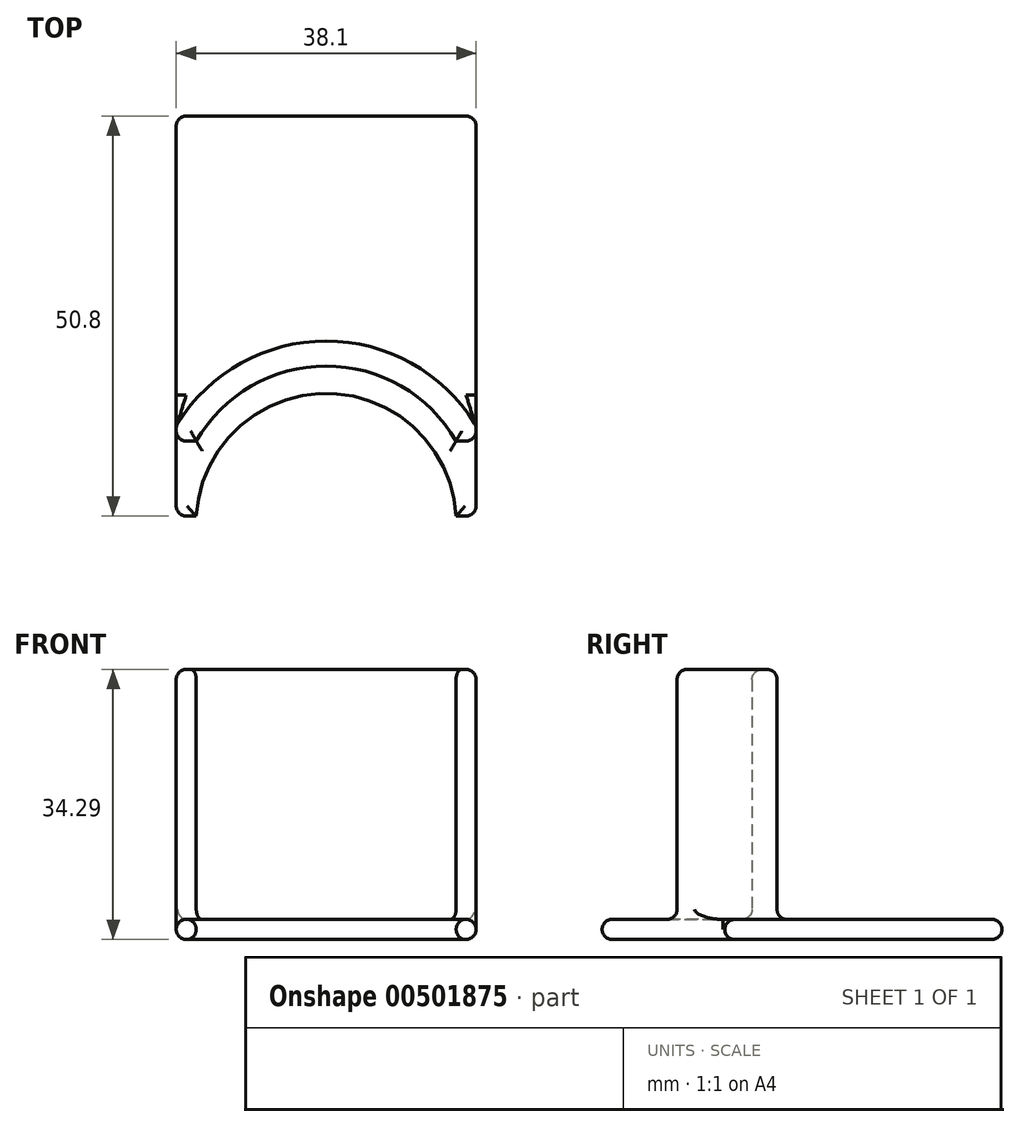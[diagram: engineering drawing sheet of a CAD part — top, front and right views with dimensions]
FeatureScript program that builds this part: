
annotation { "Feature Type Name" : "Feature", "Feature Type Description" : "" }
export const myFeature = defineFeature(function(context is Context, id is Id, definition is map)
    precondition{}
    {
        {
            var Q0;
            Q0=qCreatedBy(makeId("Top.planeOp"),FACE);
            var sketch = newSketch(context, id + "F0", { "sketchPlane" : qUnion([Q0])});
            skLineSegment(sketch, "E0.bottom", {"start": v(19.05, -19.05) * mm, "end": v(-19.05, -19.05) * mm});
            skLineSegment(sketch, "E0.top", {"start": v(19.05, 19.05) * mm, "end": v(-19.05, 19.05) * mm});
            skLineSegment(sketch, "E0.left", {"start": v(19.05, -19.05) * mm, "end": v(19.05, 19.05) * mm});
            skLineSegment(sketch, "E0.right", {"start": v(-19.05, -19.05) * mm, "end": v(-19.05, 19.05) * mm});
            skPoint(sketch, "E0.middle", {"position": v(0, 0) * mm});
            skSolve(sketch);
        }
        {
            var Q0;
            Q0=makeQuery(id+"F0.imprint","IMPRINT",FACE,{"disambiguationData":[TD([[makeQuery(id+"F0.imprint","IMPRINT",EDGE,{"derivedFrom":sQuery(id+"F0.wireOp",EDGE,"E0.bottom")}),-1.0]])]});
            extrude(context, id + "F1", {"entities" : qUnion([Q0]), "depth" : 2.54 * mm});
        }
        {
            var Q0;
            Q0=makeQuery(id+"F1.opExtrude","CAP_FACE",FACE,{"disambiguationData":[OSD([sQuery(id+"F0.wireOp",EDGE,"E0.bottom"),sQuery(id+"F0.wireOp",EDGE,"E0.top"),sQuery(id+"F0.wireOp",EDGE,"E0.left"),sQuery(id+"F0.wireOp",EDGE,"E0.right")])],"isStart":false});
            var sketch = newSketch(context, id + "F2", { "sketchPlane" : qUnion([Q0])});
            skArc(sketch, "E1", {"start": v(16.5, -9.52) * mm, "mid": v(0, 0) * mm, "end": v(-16.5, -9.53) * mm});
            skArc(sketch, "E2", {"start": v(16.5, -19.05) * mm, "mid": v(0, -3.48) * mm, "end": v(-16.51, -19.05) * mm});
            skLineSegment(sketch, "E3", {"start": v(16.5, -19.05) * mm, "end": v(-16.5, -19.05) * mm});
            skArc(sketch, "E4.0", {"start": v(19.05, -7.6) * mm, "mid": v(0, 3.18) * mm, "end": v(-19.05, -7.6) * mm});
            skLineSegment(sketch, "E5", {"start": v(19.05, -9.52) * mm, "end": v(19.05, -7.6) * mm});
            skLineSegment(sketch, "E6", {"start": v(-19.05, -9.52) * mm, "end": v(-19.05, -7.6) * mm});
            skLineSegment(sketch, "E7", {"start": v(19.05, -9.52) * mm, "end": v(16.5, -9.52) * mm});
            skLineSegment(sketch, "E8.trimOffspring", {"start": v(-16.5, -9.52) * mm, "end": v(-19.05, -9.52) * mm});
            skSolve(sketch);
        }
        {
            var Q0;
            Q0=makeQuery(id+"F2.imprint","IMPRINT",FACE,{"disambiguationData":[TD([[makeQuery(id+"F2.imprint","IMPRINT",EDGE,{"derivedFrom":sQuery(id+"F2.wireOp",EDGE,"E2")}),1.0]])]});
            extrude(context, id + "F3", {"entities" : qUnion([Q0]), "operationType" : NewBodyOperationType.REMOVE, "oppositeDirection" : true, "depth" : 25.4 * mm});
        }
        {
            var Q0;
            Q0=makeQuery(id+"F2.imprint","IMPRINT",FACE,{"disambiguationData":[TD([[makeQuery(id+"F2.imprint","IMPRINT",EDGE,{"derivedFrom":sQuery(id+"F2.wireOp",EDGE,"E1")}),-1.0]])]});
            extrude(context, id + "F4", {"entities" : qUnion([Q0]), "operationType" : NewBodyOperationType.ADD, "depth" : 31.75 * mm});
        }
        {
            var Q0;
            Q0=makeQuery(id+"F4.opExtrude","SWEPT_EDGE",EDGE,{"disambiguationData":[OSD([sQuery(id+"F0.wireOp",EDGE,"E0.left"),sQuery(id+"F2.wireOp",EDGE,"E5"),sQuery(id+"F2.wireOp",EDGE,"E7")])]});
            var Q1;
            Q1=makeQuery(id+"F4.opExtrude","SWEPT_EDGE",EDGE,{"disambiguationData":[OSD([sQuery(id+"F0.wireOp",EDGE,"E0.right"),sQuery(id+"F2.wireOp",EDGE,"E6"),sQuery(id+"F2.wireOp",EDGE,"E8.trimOffspring")])]});
            fillet(context, id + "F5", {"entities" : qUnion([Q0, Q1]), "radius" : 1.27 * mm, "tangentPropagation" : true, "allowEdgeOverflow" : false});
        }
        {
            var Q0;
            Q0=makeQuery(id+"F1.opExtrude","SWEPT_FACE",FACE,{"disambiguationData":[OSD([sQuery(id+"F0.wireOp",EDGE,"E0.top")])]});
            extrude(context, id + "F6", {"entities" : qUnion([Q0]), "operationType" : NewBodyOperationType.ADD, "depth" : 12.7 * mm});
        }
        {
            var Q0;
            {var subQ0=sQuery(id+"F0.wireOp",EDGE,"E0.top");var subQ1=sQuery(id+"F0.wireOp",EDGE,"E0.right");var subQ2=sQuery(id+"F0.wireOp",EDGE,"E0.left");Q0=makeQuery(id+"F6.boolean.opBoolean","MERGE",FACE,{"derivedFrom":[makeQuery(id+"F4.boolean.opBoolean","SPLIT",FACE,{"disambiguationData":[TD([makeQuery(id+"F1.opExtrude","SWEPT_FACE",FACE,{"disambiguationData":[OSD([subQ0])]})])],"derivedFrom":makeQuery(id+"F1.opExtrude","CAP_FACE",FACE,{"disambiguationData":[OSD([sQuery(id+"F0.wireOp",EDGE,"E0.bottom"),subQ0,subQ2,subQ1])],"isStart":false})}),makeQuery(id+"F6.opExtrude","SWEPT_FACE",FACE,{"disambiguationData":[OSD([subQ0]),TDD([makeQuery(id+"F1.opExtrude","CAP_EDGE",EDGE,{"disambiguationData":[OSD([subQ0])],"isStart":false})])]})]});}
            var Q1;
            {var subQ0=sQuery(id+"F0.wireOp",EDGE,"E0.left");Q1=makeQuery(id+"F6.boolean.opBoolean","MERGE",FACE,{"derivedFrom":[makeQuery(id+"F4.boolean.opBoolean","MERGE",FACE,{"derivedFrom":[makeQuery(id+"F1.opExtrude","SWEPT_FACE",FACE,{"disambiguationData":[OSD([subQ0])]}),makeQuery(id+"F4.opExtrude","SWEPT_FACE",FACE,{"disambiguationData":[OSD([sQuery(id+"F2.wireOp",EDGE,"E5")])]})]}),makeQuery(id+"F6.opExtrude","SWEPT_FACE",FACE,{"disambiguationData":[OSD([sQuery(id+"F0.wireOp",EDGE,"E0.top"),subQ0])]})]});}
            var Q2;
            {var subQ0=sQuery(id+"F0.wireOp",EDGE,"E0.top");Q2=makeQuery(id+"F6.boolean.opBoolean","MERGE",FACE,{"derivedFrom":[makeQuery(id+"F1.opExtrude","CAP_FACE",FACE,{"disambiguationData":[OSD([sQuery(id+"F0.wireOp",EDGE,"E0.bottom"),subQ0,sQuery(id+"F0.wireOp",EDGE,"E0.left"),sQuery(id+"F0.wireOp",EDGE,"E0.right")])],"isStart":true}),makeQuery(id+"F6.opExtrude","SWEPT_FACE",FACE,{"disambiguationData":[OSD([subQ0]),TDD([makeQuery(id+"F1.opExtrude","CAP_EDGE",EDGE,{"disambiguationData":[OSD([subQ0])],"isStart":true})])]})]});}
            var Q3;
            Q3=makeQuery(id+"F6.opExtrude","CAP_FACE",FACE,{"disambiguationData":[OSD([sQuery(id+"F0.wireOp",EDGE,"E0.top")])],"isStart":false});
            var Q4;
            {var subQ0=sQuery(id+"F0.wireOp",EDGE,"E0.right");Q4=makeQuery(id+"F6.boolean.opBoolean","MERGE",FACE,{"derivedFrom":[makeQuery(id+"F4.boolean.opBoolean","MERGE",FACE,{"derivedFrom":[makeQuery(id+"F1.opExtrude","SWEPT_FACE",FACE,{"disambiguationData":[OSD([subQ0])]}),makeQuery(id+"F4.opExtrude","SWEPT_FACE",FACE,{"disambiguationData":[OSD([sQuery(id+"F2.wireOp",EDGE,"E6")])]})]}),makeQuery(id+"F6.opExtrude","SWEPT_FACE",FACE,{"disambiguationData":[OSD([sQuery(id+"F0.wireOp",EDGE,"E0.top"),subQ0])]})]});}
            var Q5;
            Q5=makeQuery(id+"F4.opExtrude","CAP_FACE",FACE,{"disambiguationData":[OSD([sQuery(id+"F2.wireOp",EDGE,"E1"),sQuery(id+"F2.wireOp",EDGE,"E4.0"),sQuery(id+"F2.wireOp",EDGE,"E5"),sQuery(id+"F2.wireOp",EDGE,"E6"),sQuery(id+"F2.wireOp",EDGE,"E7"),sQuery(id+"F2.wireOp",EDGE,"E8.trimOffspring")])],"isStart":false});
            var Q6;
            {var subQ0=sQuery(id+"F0.wireOp",EDGE,"E0.right");var subQ1=sQuery(id+"F0.wireOp",EDGE,"E0.left");var subQ2=sQuery(id+"F0.wireOp",EDGE,"E0.bottom");Q6=makeQuery(id+"F4.boolean.opBoolean","SPLIT",FACE,{"disambiguationData":[TD([makeQuery(id+"F1.opExtrude","SWEPT_FACE",FACE,{"disambiguationData":[OSD([subQ2])]})])],"derivedFrom":makeQuery(id+"F1.opExtrude","CAP_FACE",FACE,{"disambiguationData":[OSD([subQ2,sQuery(id+"F0.wireOp",EDGE,"E0.top"),subQ1,subQ0])],"isStart":false})});}
            fillet(context, id + "F7", {"entities" : qUnion([Q0, Q1, Q2, Q3, Q4, Q5, Q6]), "radius" : 1.27 * mm, "tangentPropagation" : true, "allowEdgeOverflow" : false});
        }
    });
